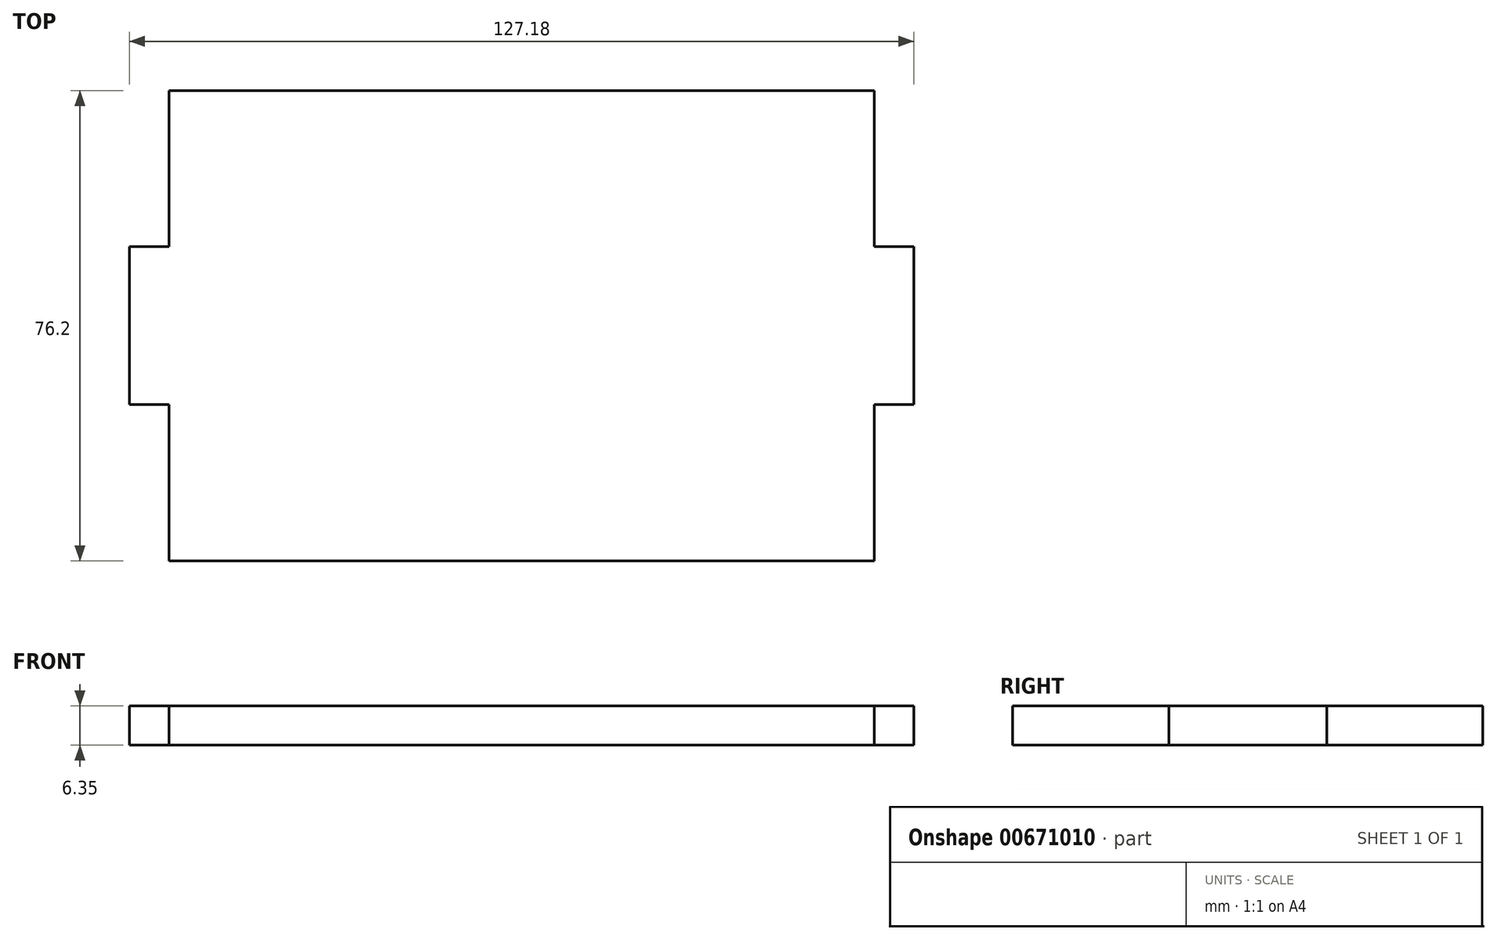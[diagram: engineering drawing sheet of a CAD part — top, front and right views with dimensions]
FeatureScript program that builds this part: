
annotation { "Feature Type Name" : "Feature", "Feature Type Description" : "" }
export const myFeature = defineFeature(function(context is Context, id is Id, definition is map)
    precondition{}
    {
        {
            var Q0;
            Q0=qCreatedBy(makeId("Top.planeOp"),FACE);
            var sketch = newSketch(context, id + "F0", { "sketchPlane" : qUnion([Q0])});
            skLineSegment(sketch, "E0.bottom", {"start": v(0, 0) * mm, "end": v(114.3, 0) * mm});
            skLineSegment(sketch, "E0.top", {"start": v(0, 76.2) * mm, "end": v(114.3, 76.2) * mm});
            skLineSegment(sketch, "E0.left", {"start": v(0, 0) * mm, "end": v(0, 76.2) * mm});
            skLineSegment(sketch, "E0.right", {"start": v(114.3, 0) * mm, "end": v(114.3, 76.2) * mm});
            skLineSegment(sketch, "E1.bottom", {"start": v(114.3, 50.89) * mm, "end": v(120.74, 50.89) * mm});
            skLineSegment(sketch, "E1.top", {"start": v(114.3, 25.31) * mm, "end": v(120.74, 25.31) * mm});
            skLineSegment(sketch, "E1.left", {"start": v(114.3, 50.89) * mm, "end": v(114.3, 25.31) * mm});
            skLineSegment(sketch, "E1.right", {"start": v(120.74, 50.89) * mm, "end": v(120.74, 25.31) * mm});
            skLineSegment(sketch, "E2.bottom", {"start": v(0, 50.89) * mm, "end": v(-6.44, 50.89) * mm});
            skLineSegment(sketch, "E2.top", {"start": v(0, 25.31) * mm, "end": v(-6.44, 25.31) * mm});
            skLineSegment(sketch, "E2.left", {"start": v(0, 50.89) * mm, "end": v(0, 25.31) * mm});
            skLineSegment(sketch, "E2.right", {"start": v(-6.44, 50.89) * mm, "end": v(-6.44, 25.31) * mm});
            skLineSegment(sketch, "E3.bottom", {"start": v(18.96, 0) * mm, "end": v(44.54, 0) * mm});
            skLineSegment(sketch, "E3.top", {"start": v(18.96, -6.44) * mm, "end": v(44.54, -6.44) * mm});
            skLineSegment(sketch, "E3.left", {"start": v(18.96, 0) * mm, "end": v(18.96, -6.44) * mm});
            skLineSegment(sketch, "E3.right", {"start": v(44.54, 0) * mm, "end": v(44.54, -6.44) * mm});
            skLineSegment(sketch, "E4.bottom", {"start": v(69.76, 0) * mm, "end": v(95.34, 0) * mm});
            skLineSegment(sketch, "E4.top", {"start": v(69.76, -6.44) * mm, "end": v(95.34, -6.44) * mm});
            skLineSegment(sketch, "E4.left", {"start": v(69.76, 0) * mm, "end": v(69.76, -6.44) * mm});
            skLineSegment(sketch, "E4.right", {"start": v(95.34, 0) * mm, "end": v(95.34, -6.44) * mm});
            skPoint(sketch, "E5", {"position": v(-6.44, 38.1) * mm});
            skPoint(sketch, "E6", {"position": v(31.75, -6.44) * mm});
            skPoint(sketch, "E7", {"position": v(82.55, -6.44) * mm});
            skPoint(sketch, "E8", {"position": v(120.74, 38.1) * mm});
            skSolve(sketch);
        }
        {
            var Q0;
            {var subQ2=sQuery(id+"F0.wireOp",EDGE,"E0.top");Q0=makeQuery(id+"F0.imprint","IMPRINT",FACE,{"disambiguationData":[TD([[makeQuery(id+"F0.imprint","IMPRINT",EDGE,{"derivedFrom":subQ2}),-1.0]])]});}
            var Q1;
            Q1=makeQuery(id+"F0.imprint","IMPRINT",FACE,{"disambiguationData":[TD([[makeQuery(id+"F0.imprint","IMPRINT",EDGE,{"derivedFrom":sQuery(id+"F0.wireOp",EDGE,"E2.bottom")}),1.0]])]});
            var Q2;
            Q2=makeQuery(id+"F0.imprint","IMPRINT",FACE,{"disambiguationData":[TD([[makeQuery(id+"F0.imprint","IMPRINT",EDGE,{"derivedFrom":sQuery(id+"F0.wireOp",EDGE,"E3.bottom")}),-1.0]])]});
            var Q3;
            Q3=makeQuery(id+"F0.imprint","IMPRINT",FACE,{"disambiguationData":[TD([[makeQuery(id+"F0.imprint","IMPRINT",EDGE,{"derivedFrom":sQuery(id+"F0.wireOp",EDGE,"E4.bottom")}),-1.0]])]});
            var Q4;
            Q4=makeQuery(id+"F0.imprint","IMPRINT",FACE,{"disambiguationData":[TD([[makeQuery(id+"F0.imprint","IMPRINT",EDGE,{"derivedFrom":sQuery(id+"F0.wireOp",EDGE,"E1.bottom")}),-1.0]])]});
            extrude(context, id + "F1", {"entities" : qUnion([Q0, Q1, Q2, Q3, Q4]), "depth" : 6.35 * mm, "offsetDistance" : 25.4 * mm});
        }
    });
